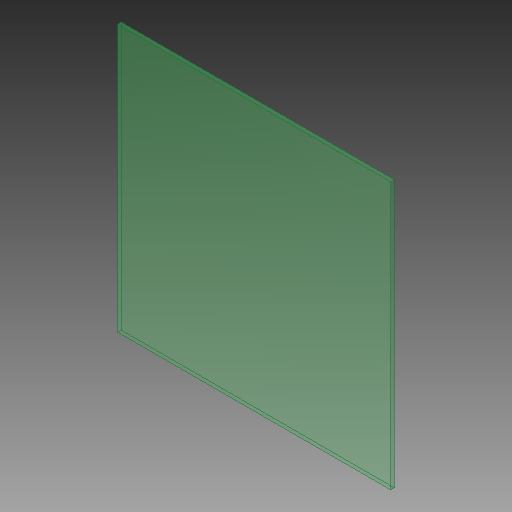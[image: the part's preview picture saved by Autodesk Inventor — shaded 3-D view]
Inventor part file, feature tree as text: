
AUTODESK INVENTOR PART (.ipt)
format: ipt  version: 2018.1 (Build 221171000, 171)  size: 94,720 bytes
history: native  units: mm
features: other x1, extrude x1, sketch x1
ambient origin geometry x8: Origin, YZ Plane, XZ Plane, XY Plane, X Axis, Y Axis, Z Axis, Center Point
bodies: Solid1 (feature_tree)
feature tree (3):
  parser-record x1  (decoder bookkeeping rows leaked as tree rows — omitted from the tree; the rows remain in map.json)
  extrude  "Extrusion1"  Depth=370.0mm
  sketch  "Sketch1"  dims[d0=379.0mm d1=370.0mm d2=5.0mm d3=0.0mm]
note: 1 file-system path scrubbed to <path> (originals preserved in map.json)
